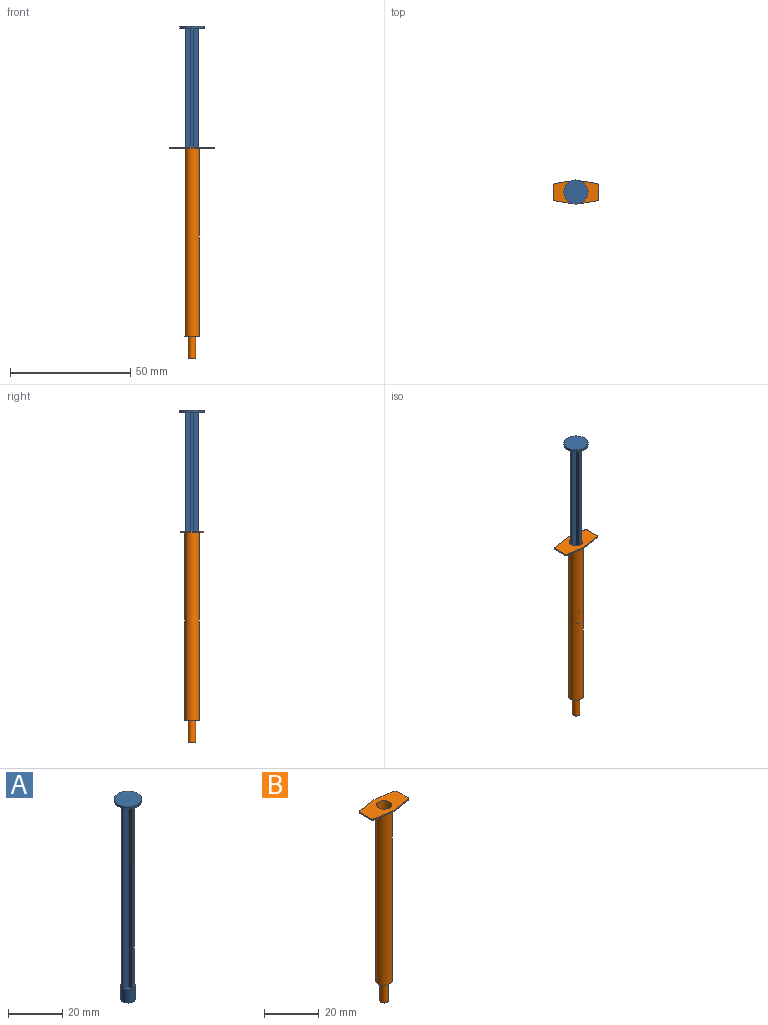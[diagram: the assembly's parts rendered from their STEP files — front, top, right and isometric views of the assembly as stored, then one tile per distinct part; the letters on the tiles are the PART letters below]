
ASSEMBLY  parts=2 mates=1
PART A: 18 faces, bbox 10x10x90 mm
  f0: cylinder r=2.7mm len=6mm, axis (0,0,-1), area 101.8mm2, adj f1,f2
  f1: plane 5.4x5.4mm, normal (0,0,1), area 13.4mm2, adj f0,f3,f4,f5,f6,f7,f8,f9
  f2: plane 5.4x5.4mm, normal (0,0,-1), area 22.9mm2, adj f0
  f3: plane 83x2.12mm, normal (-1,0,0), area 175.5mm2, adj f1,f4,f14,f15
  f4: plane 83x1mm, normal (0,-1,0), area 83mm2, adj f1,f3,f5,f15
  f5: plane 83x2.12mm, normal (1,0,0), area 175.5mm2, adj f1,f4,f6,f15
  f6: plane 83x2.13mm, normal (0,-1,0), area 176.4mm2, adj f1,f5,f7,f15
  f7: plane 83x1mm, normal (1,0,0), area 83mm2, adj f1,f6,f8,f15
  f8: plane 83x2.13mm, normal (0,1,0), area 176.4mm2, adj f1,f7,f9,f15
  f9: plane 83x2.12mm, normal (1,0,0), area 175.5mm2, adj f1,f8,f10,f15
  f10: plane 83x1mm, normal (0,1,0), area 83mm2, adj f1,f9,f11,f15
  f11: plane 83x2.12mm, normal (-1,0,0), area 175.5mm2, adj f1,f10,f12,f15
  f12: plane 83x2.13mm, normal (0,1,0), area 176.4mm2, adj f1,f11,f13,f15
  f13: plane 83x1mm, normal (-1,0,0), area 83mm2, adj f1,f12,f14,f15
  f14: plane 83x2.13mm, normal (0,-1,0), area 176.4mm2, adj f1,f3,f13,f15
  f15: plane 10x10mm, normal (0,0,-1), area 69.1mm2, adj f3,f4,f5,f6,f7,f8,f9,f10
  f16: cylinder r=5mm len=10mm, axis (0,0,-1), area 31.4mm2, adj f15,f17
  f17: plane 10x10mm, normal (0,0,1), area 78.5mm2, adj f16
PART B: 24 faces, bbox 19x9.9x87.5 mm
  f0: plane 1x1mm, normal (0,0,-1), area 0.8mm2, adj f1
  f1: cylinder r=0.5mm len=7mm, axis (0,0,1), area 22mm2, adj f0,f2
  f2: plane 2.2x2.2mm, normal (0,0,-1), area 3mm2, adj f1,f3
  f3: cylinder r=1.1mm len=7mm, axis (0,0,1), area 48.4mm2, adj f2,f4
  f4: plane 3x3mm, normal (0,0,-1), area 3.3mm2, adj f3,f5
  f5: cylinder r=1.5mm len=9mm, axis (0,0,1), area 84.8mm2, adj f4,f6
  f6: plane 6x6mm, normal (0,0,-1), area 21.2mm2, adj f5,f7
  f7: cylinder r=3mm len=78mm, axis (0,0,1), area 1470.3mm2, adj f6,f21
  f8: plane 7.72x1.22mm, normal (-0.16,0.99,0), area 3.9mm2, adj f9,f19,f20,f21
  f9: cylinder r=1mm len=0.99mm, axis (0,0,-1), area 0.7mm2, adj f8,f10,f20,f21
  f10: plane 5.29x0.5mm, normal (-1,0,0), area 2.6mm2, adj f9,f11,f20,f21
  f11: cylinder r=1mm len=0.99mm, axis (0,0,-1), area 0.7mm2, adj f10,f12,f20,f21
  f12: plane 7.72x1.22mm, normal (-0.16,-0.99,0), area 3.9mm2, adj f11,f13,f20,f21
  f13: cylinder r=6mm len=1.87mm, axis (0,0,-1), area 0.9mm2, adj f12,f14,f20,f21
  f14: plane 7.72x1.22mm, normal (0.16,-0.99,0), area 3.9mm2, adj f13,f15,f20,f21
  f15: cylinder r=1mm len=0.99mm, axis (0,0,-1), area 0.7mm2, adj f14,f16,f20,f21
  f16: plane 5.29x0.5mm, normal (1,0,0), area 2.6mm2, adj f15,f17,f20,f21
  f17: cylinder r=1mm len=0.99mm, axis (0,0,-1), area 0.7mm2, adj f16,f18,f20,f21
  f18: plane 7.72x1.22mm, normal (0.16,0.99,0), area 3.9mm2, adj f17,f19,f20,f21
  f19: cylinder r=6mm len=1.87mm, axis (0,0,-1), area 0.9mm2, adj f8,f18,f20,f21
  f20: plane 19x9.85mm, normal (0,0,1), area 137.9mm2, adj f8,f9,f10,f11,f12,f13,f14,f15
  f21: plane 19x9.85mm, normal (0,0,-1), area 132.5mm2, adj f7,f8,f9,f10,f11,f12,f13,f14
  f22: plane 5.4x5.4mm, normal (0,0,1), area 22.9mm2, adj f23
  f23: cylinder r=2.7mm len=78.4mm, axis (0,0,1), area 1330mm2, adj f20,f22
PLACE A t=(-36.42,-9.84,30.83)mm
PLACE B t=(-50.01,-9.84,-8.07)mm
MATE slider A.f0 <-> B.f1  axis (0,0,-1) through (-50.01,-9.84,30.93)mm
